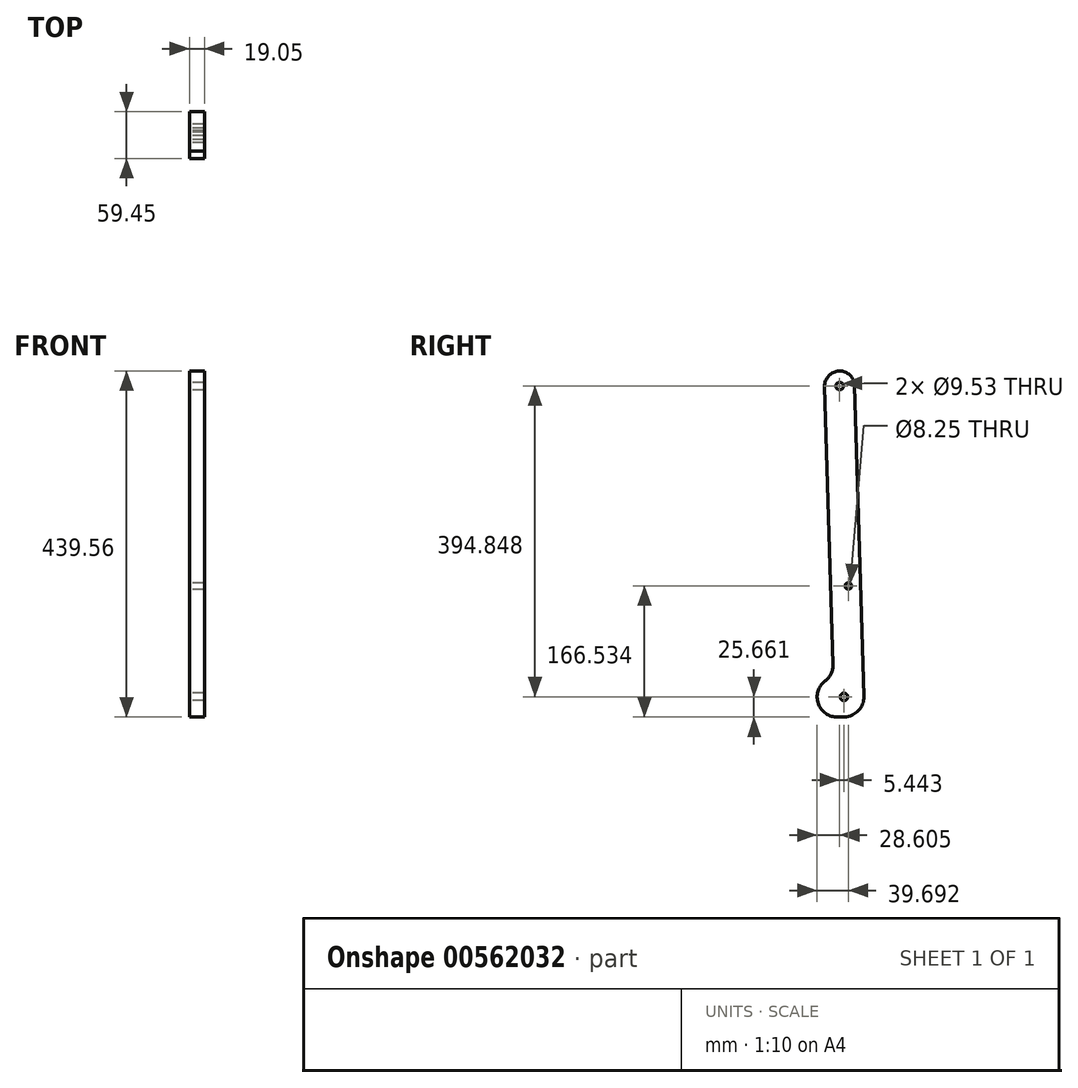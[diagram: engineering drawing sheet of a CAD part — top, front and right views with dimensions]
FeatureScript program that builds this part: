
annotation { "Feature Type Name" : "Feature", "Feature Type Description" : "" }
export const myFeature = defineFeature(function(context is Context, id is Id, definition is map)
    precondition{}
    {
        {
            var Q0;
            Q0=qCreatedBy(makeId("Right.planeOp"),FACE);
            var sketch = newSketch(context, id + "F0", { "sketchPlane" : qUnion([Q0])});
            skLineSegment(sketch, "E0", {"start": v(-513.86, 319.86) * mm, "end": v(-513.86, 78.56) * mm});
            skSolve(sketch);
        }
        {
            var Q0;
            Q0=qCreatedBy(makeId("Right.planeOp"),FACE);
            var sketch = newSketch(context, id + "F1", { "sketchPlane" : qUnion([Q0])});
            skLineSegment(sketch, "E1", {"start": v(-749.76, 256.37) * mm, "end": v(-601.81, 261.03) * mm});
            skLineSegment(sketch, "E2", {"start": v(-560.54, 653.66) * mm, "end": v(-601.81, 261.03) * mm});
            skLineSegment(sketch, "E3", {"start": v(-560.54, 653.66) * mm, "end": v(-749.76, 256.37) * mm});
            skLineSegment(sketch, "E4", {"start": v(-712.77, 291.22) * mm, "end": v(-723.7, 436.42) * mm});
            skLineSegment(sketch, "E5", {"start": v(-712.77, 291.22) * mm, "end": v(-826.16, 542.64) * mm});
            skLineSegment(sketch, "E6", {"start": v(-723.7, 436.42) * mm, "end": v(-826.16, 542.64) * mm});
            skLineSegment(sketch, "E7", {"start": v(-1007.93, 660.27) * mm, "end": v(-826.16, 542.64) * mm});
            skLineSegment(sketch, "E8", {"start": v(-1037.12, 677.37) * mm, "end": v(-1007.93, 660.27) * mm});
            skLineSegment(sketch, "E9", {"start": v(-1037.12, 677.37) * mm, "end": v(-712.77, 291.22) * mm});
            skLineSegment(sketch, "E10", {"start": v(-1007.93, 660.27) * mm, "end": v(-712.77, 291.22) * mm});
            skLineSegment(sketch, "E11", {"start": v(-601.81, 261.03) * mm, "end": v(-595.01, 401.75) * mm});
            skLineSegment(sketch, "E12", {"start": v(-601.81, 261.03) * mm, "end": v(-607.25, 655.88) * mm});
            skLineSegment(sketch, "E13", {"start": v(-595.01, 401.75) * mm, "end": v(-607.25, 655.88) * mm});
            skLineSegment(sketch, "E14", {"start": v(-723.7, 436.42) * mm, "end": v(-595.01, 401.75) * mm});
            skLineSegment(sketch, "E15", {"start": v(-826.16, 542.64) * mm, "end": v(-774.61, 590.25) * mm});
            skLineSegment(sketch, "E16", {"start": v(-749.76, 256.37) * mm, "end": v(-774.61, 590.25) * mm});
            skLineSegment(sketch, "E17", {"start": v(-1041.29, 793.41) * mm, "end": v(-774.61, 590.25) * mm});
            skLineSegment(sketch, "E18", {"start": v(-1390.78, 317.95) * mm, "end": v(-1336.8, 360.93) * mm});
            skLineSegment(sketch, "E19", {"start": v(-1336.8, 360.93) * mm, "end": v(-1295.1, 301.57) * mm});
            skLineSegment(sketch, "E20", {"start": v(-1041.29, 793.41) * mm, "end": v(-1295.1, 301.57) * mm});
            skLineSegment(sketch, "E21", {"start": v(-1295.1, 301.57) * mm, "end": v(-1037.12, 677.37) * mm});
            skLineSegment(sketch, "E22", {"start": v(-1037.12, 677.37) * mm, "end": v(-1041.29, 793.41) * mm});
            skLineSegment(sketch, "E23", {"start": v(-1007.93, 660.27) * mm, "end": v(-1336.8, 360.93) * mm});
            skLineSegment(sketch, "E24", {"start": v(-1390.78, 317.95) * mm, "end": v(-1295.1, 301.57) * mm});
            skLineSegment(sketch, "E25", {"start": v(-1295.1, 301.57) * mm, "end": v(-1295.1, 192.57) * mm});
            skLineSegment(sketch, "E26", {"start": v(-1295.1, 192.57) * mm, "end": v(-1403.22, 211.07) * mm});
            skLineSegment(sketch, "E27", {"start": v(-1403.22, 211.07) * mm, "end": v(-1390.78, 317.95) * mm});
            skLineSegment(sketch, "E28", {"start": v(-1390.78, 317.95) * mm, "end": v(-1295.1, 192.57) * mm});
            skLineSegment(sketch, "E29", {"start": v(0, 0) * mm, "end": v(0, 674.17) * mm});
            skLineSegment(sketch, "E30", {"start": v(-316.61, 320.6) * mm, "end": v(-316.61, 307.94) * mm});
            skLineSegment(sketch, "E31", {"start": v(-400.45, 218.07) * mm, "end": v(-378.01, 218.07) * mm});
            skLineSegment(sketch, "E32", {"start": v(-472.6, 74.76) * mm, "end": v(-472.6, 54.94) * mm});
            skSolve(sketch);
        }
        {
            var Q0;
            Q0=qCreatedBy(makeId("Right.planeOp"),FACE);
            var sketch = newSketch(context, id + "F2", { "sketchPlane" : qUnion([Q0])});
            skArc(sketch, "E33", {"start": v(-609.69, 235.38) * mm, "mid": v(-634.4, 252.32) * mm, "end": v(-625.8, 281.02) * mm});
            skArc(sketch, "E34", {"start": v(-626.3, 655.3) * mm, "mid": v(-607.82, 674.92) * mm, "end": v(-588.21, 656.45) * mm});
            skLineSegment(sketch, "E35", {"start": v(-615.74, 302.02) * mm, "end": v(-626.3, 655.3) * mm});
            skLineSegment(sketch, "E36", {"start": v(-588.21, 656.45) * mm, "end": v(-576.42, 261.79) * mm});
            skLineSegment(sketch, "E37", {"start": v(-609.69, 235.38) * mm, "end": v(-601.05, 235.64) * mm});
            skPoint(sketch, "E38.visualSharp", {"position": v(-575.66, 236.4) * mm});
            skArc(sketch, "E38.filletArc", {"start": v(-601.05, 235.64) * mm, "mid": v(-583.32, 243.62) * mm, "end": v(-576.42, 261.79) * mm});
            skPoint(sketch, "E39.visualSharp", {"position": v(-614.9, 273.75) * mm});
            skArc(sketch, "E39.filletArc", {"start": v(-625.8, 281.02) * mm, "mid": v(-618.22, 290.3) * mm, "end": v(-615.74, 302.02) * mm});
            skCircle(sketch, "E40", {"center": v(-601.81, 261.03) * mm, "radius": 4.76 * mm});
            skCircle(sketch, "E41", {"center": v(-607.25, 655.88) * mm, "radius": 4.76 * mm});
            skCircle(sketch, "E42", {"center": v(-596.17, 401.9) * mm, "radius": 4.13 * mm});
            skSolve(sketch);
        }
        {
            var Q0;
            Q0=qSketchRegion(id+"F2",true);
            extrude(context, id + "F3", {"entities" : qUnion([Q0]), "depth" : 19.05 * mm, "offsetDistance" : 25.4 * mm});
        }
    });
